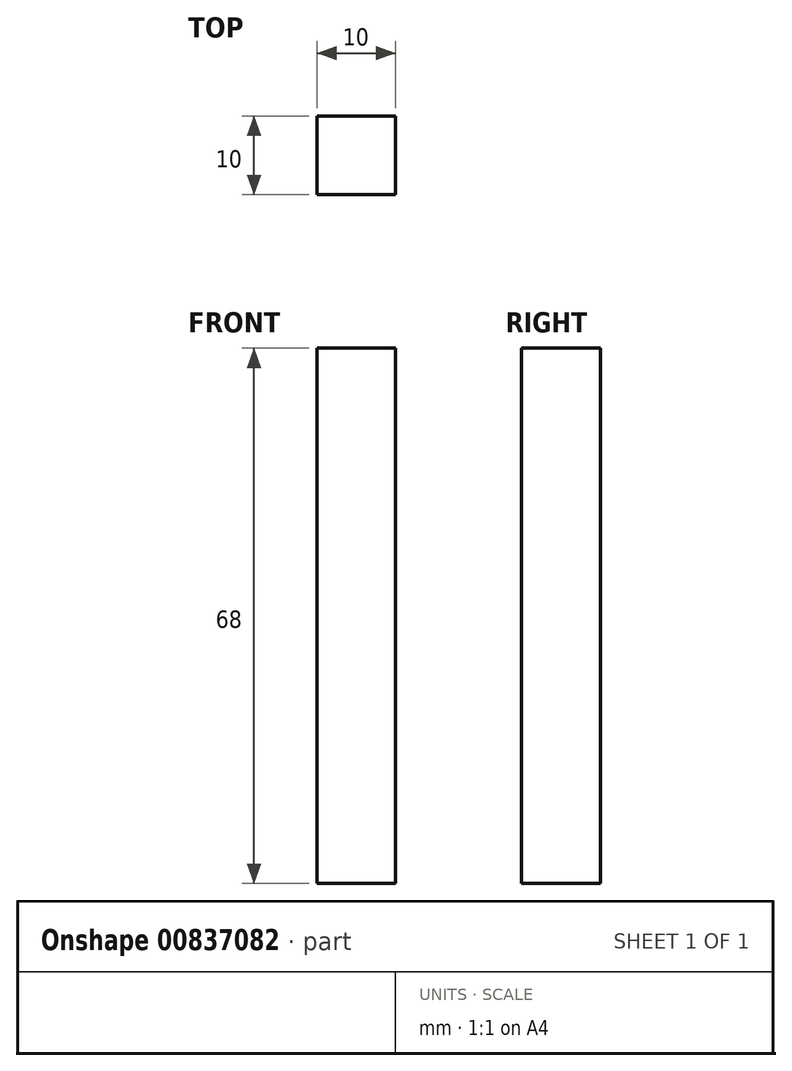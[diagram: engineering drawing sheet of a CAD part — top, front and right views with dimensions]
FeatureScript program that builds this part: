
annotation { "Feature Type Name" : "Feature", "Feature Type Description" : "" }
export const myFeature = defineFeature(function(context is Context, id is Id, definition is map)
    precondition{}
    {
        {
            var Q0;
            Q0=qCreatedBy(makeId("Top.planeOp"),FACE);
            var sketch = newSketch(context, id + "F0", { "sketchPlane" : qUnion([Q0])});
            skLineSegment(sketch, "E0.bottom", {"start": v(-5, 5) * mm, "end": v(5, 5) * mm});
            skLineSegment(sketch, "E0.top", {"start": v(-5, -5) * mm, "end": v(5, -5) * mm});
            skLineSegment(sketch, "E0.left", {"start": v(-5, 5) * mm, "end": v(-5, -5) * mm});
            skLineSegment(sketch, "E0.right", {"start": v(5, 5) * mm, "end": v(5, -5) * mm});
            skPoint(sketch, "E0.middle", {"position": v(0, 0) * mm});
            skSolve(sketch);
        }
        {
            var Q0;
            Q0=makeQuery(id+"F0.imprint","IMPRINT",FACE,{"disambiguationData":[TD([[makeQuery(id+"F0.imprint","IMPRINT",EDGE,{"derivedFrom":sQuery(id+"F0.wireOp",EDGE,"E0.bottom")}),-1.0]])]});
            extrude(context, id + "F1", {"entities" : qUnion([Q0]), "depth" : 68 * mm, "offsetDistance" : 25 * mm});
        }
    });
